# Revit family: Casement_41_E_Side_Hung_HD_Standard
name_source: partatom
category: Windows
revit_build: Autodesk Revit 2014 (Build: 20130308_1515(x64)
units: mm (PartAtom-declared; Revit-internal decimal feet)

## types (18) — shared parameters
Corrected Mullion Configuration = 2 mm  [stored 0.00656168 ft]
Custom Sash Height = 1102 mm
Custom Sash Width = 502 mm
Description = Window 41mm, Type E, Side hung, Heavy duty sash
Frame Profile Thickness = 41 mm  [stored 0.134514 ft]
Heavy Duty Sash = Yes
Limit Fixed Pane Height Max = 3000 mm  [stored 9.84252 ft]
Limit Fixed Pane Height Min = 200 mm  [stored 0.656168 ft]
Limit Fixed Pane Width Max = 3000 mm  [stored 9.84252 ft]
Limit Fixed Pane Width Min = 200 mm  [stored 0.656168 ft]
Limit Sash Height Max = 1500 mm  [stored 4.92126 ft]
Limit Sash Height Min = 300 mm  [stored 0.984252 ft]
Limit Sash Width Max = 700 mm  [stored 2.29659 ft]
Limit Sash Width Min = 300 mm  [stored 0.984252 ft]
Manufacturer = Crealco
Max System DG Unit Thickness = 25 mm  [stored 0.082021 ft]
Model = Casement 41
Rough Width = 3 mm  [stored 0.00984252 ft]
Sash Side Gap = 44 mm
Standard Mullion Different = No
Standard Sash = No
URL = http://www.crealco.co.za
Wall Closure = By host
zero-valued in all types: Custom Frame Offset From Exterior

## per-type parameters (varying)
| type | Clearvue Insulated LowE SHGC Value | Clearvue Insulated LowE U Value | Clearvue Insulated SHGC Value | Clearvue Insulated U Value | Clearvue SHGC Value | Clearvue U Value | Custom Windload | Custom Window Height | Custom Window Width | Energy Advantage SHGC Value | Energy Advantage U Value | Intruderprufe Insulated LowE SHGC Value | Intruderprufe Insulated LowE U Value | Intruderprufe Insulated SHGC Value | Intruderprufe Insulated U Value | Intruderprufe LowE SHGC Value | Intruderprufe LowE U Value | Intruderprufe SHGC Value | Intruderprufe U Value | Toughened Safety SHGC Value | Toughened Safety U Value |
| 41-0915S-HD-1000Pa | 0.699 | 4.27 | 0.699 | 4.38 | 0.517 | 6.07 | 1000 mm  [stored 3.28084 ft] | 1490 mm  [stored 4.88845 ft] | 890 mm  [stored 2.91995 ft] | 0.466 | 4.99 | 0.581 | 3.25 | 0.581 | 3.32 | 0.433 | 4.83 | 0.487 | 5.9 | 0.517 | 6.07 |
| 41-0915S-HD-1500Pa | 0.699 | 4.27 | 0.699 | 4.38 | 0.517 | 6.07 | 1500 mm  [stored 4.92126 ft] | 1490 mm  [stored 4.88845 ft] | 890 mm  [stored 2.91995 ft] | 0.466 | 4.99 | 0.581 | 3.25 | 0.581 | 3.32 | 0.433 | 4.83 | 0.487 | 5.9 | 0.517 | 6.07 |
| 41-0915S-HD-2000Pa | 0.699 | 4.27 | 0.699 | 4.38 | 0.517 | 6.07 | 2000 mm  [stored 6.56168 ft] | 1490 mm  [stored 4.88845 ft] | 890 mm  [stored 2.91995 ft] | 0.466 | 4.99 | 0.581 | 3.25 | 0.581 | 3.32 | 0.433 | 4.83 | 0.487 | 5.9 | 0.517 | 6.07 |
| 41-1215S-HD-1000Pa | 0.737 | 4.55 | 0.737 | 4.63 | 0.585 | 6.04 | 1000 mm  [stored 3.28084 ft] | 1490 mm  [stored 4.88845 ft] | 1190 mm  [stored 3.9042 ft] | 0.526 | 4.73 | 0.612 | 3.27 | 0.612 | 3.32 | 0.489 | 4.58 | 0.551 | 5.86 | 0.585 | 6.04 |
| 41-1215S-HD-1500Pa | 0.737 | 4.55 | 0.737 | 4.63 | 0.585 | 6.04 | 1500 mm  [stored 4.92126 ft] | 1490 mm  [stored 4.88845 ft] | 1190 mm  [stored 3.9042 ft] | 0.526 | 4.73 | 0.612 | 3.27 | 0.612 | 3.32 | 0.489 | 4.58 | 0.551 | 5.86 | 0.585 | 6.04 |
| 41-1215S-HD-2000Pa | 0.738 | 4.69 | 0.738 | 4.77 | 0.576 | 6.1 | 2000 mm  [stored 6.56168 ft] | 1490 mm  [stored 4.88845 ft] | 1190 mm  [stored 3.9042 ft] | 0.518 | 4.84 | 0.614 | 3.4 | 0.614 | 3.45 | 0.481 | 4.68 | 0.542 | 5.92 | 0.576 | 6.1 |
| 41-1515S-HD-1000Pa | 0.76 | 4.72 | 0.76 | 4.78 | 0.626 | 6.01 | 1000 mm  [stored 3.28084 ft] | 1490 mm  [stored 4.88845 ft] | 1490 mm  [stored 4.88845 ft] | 0.561 | 4.58 | 0.631 | 3.28 | 0.631 | 3.32 | 0.522 | 4.43 | 0.589 | 5.84 | 0.626 | 6.01 |
| 41-1515S-HD-1500Pa | 0.76 | 4.72 | 0.76 | 4.78 | 0.626 | 6.01 | 1500 mm  [stored 4.92126 ft] | 1490 mm  [stored 4.88845 ft] | 1490 mm  [stored 4.88845 ft] | 0.561 | 4.58 | 0.631 | 3.28 | 0.631 | 3.32 | 0.522 | 4.43 | 0.589 | 5.84 | 0.626 | 6.01 |
| 41-1515S-HD-2000Pa | 0.761 | 4.83 | 0.761 | 4.89 | 0.619 | 6.07 | 2000 mm  [stored 6.56168 ft] | 1490 mm  [stored 4.88845 ft] | 1490 mm  [stored 4.88845 ft] | 0.555 | 4.66 | 0.632 | 3.38 | 0.632 | 3.42 | 0.516 | 4.51 | 0.582 | 5.89 | 0.619 | 6.07 |
| 41-0918S-HD-1000Pa | 0.708 | 4.33 | 0.708 | 4.44 | 0.54 | 6.06 | 1000 mm  [stored 3.28084 ft] | 1790 mm  [stored 5.8727 ft] | 890 mm  [stored 2.91995 ft] | 0.486 | 4.91 | 0.589 | 3.26 | 0.589 | 3.33 | 0.452 | 4.74 | 0.508 | 5.87 | 0.54 | 6.06 |
| 41-0918S-HD-1500Pa | 0.71 | 4.52 | 0.71 | 4.62 | 0.523 | 6.16 | 1500 mm  [stored 4.92126 ft] | 1790 mm  [stored 5.8727 ft] | 890 mm  [stored 2.91995 ft] | 0.471 | 5.07 | 0.591 | 3.44 | 0.591 | 3.5 | 0.438 | 4.89 | 0.492 | 5.96 | 0.523 | 6.16 |
| 41-0918S-HD-2000Pa | 0.71 | 4.52 | 0.71 | 4.62 | 0.523 | 6.16 | 2000 mm  [stored 6.56168 ft] | 1790 mm  [stored 5.8727 ft] | 890 mm  [stored 2.91995 ft] | 0.471 | 5.07 | 0.591 | 3.44 | 0.591 | 3.5 | 0.438 | 4.89 | 0.492 | 5.96 | 0.523 | 6.16 |
| 41-1218S-HD-1000Pa | 0.744 | 4.62 | 0.744 | 4.7 | 0.605 | 6.03 | 1000 mm  [stored 3.28084 ft] | 1790 mm  [stored 5.8727 ft] | 1190 mm  [stored 3.9042 ft] | 0.543 | 4.66 | 0.618 | 3.29 | 0.618 | 3.34 | 0.505 | 4.5 | 0.569 | 5.84 | 0.605 | 6.03 |
| 41-1218S-HD-1500Pa | 0.745 | 4.76 | 0.745 | 4.83 | 0.592 | 6.1 | 1500 mm  [stored 4.92126 ft] | 1790 mm  [stored 5.8727 ft] | 1190 mm  [stored 3.9042 ft] | 0.532 | 4.78 | 0.619 | 3.42 | 0.619 | 3.47 | 0.494 | 4.62 | 0.557 | 5.91 | 0.592 | 6.1 |
| 41-1218S-HD-2000Pa | 0.745 | 4.76 | 0.745 | 4.83 | 0.592 | 6.1 | 2000 mm  [stored 6.56168 ft] | 1790 mm  [stored 5.8727 ft] | 1190 mm  [stored 3.9042 ft] | 0.532 | 4.78 | 0.619 | 3.42 | 0.619 | 3.47 | 0.494 | 4.62 | 0.557 | 5.91 | 0.592 | 6.1 |
| 41-1518S-HD-1000Pa | 0.766 | 4.9 | 0.766 | 4.96 | 0.633 | 6.06 | 1000 mm  [stored 3.28084 ft] | 1790 mm  [stored 5.8727 ft] | 1490 mm  [stored 4.88845 ft] | 0.568 | 4.61 | 0.637 | 3.41 | 0.637 | 3.45 | 0.528 | 4.45 | 0.596 | 5.87 | 0.633 | 6.06 |
| 41-1518S-HD-1500Pa | 0.766 | 4.9 | 0.766 | 4.96 | 0.633 | 6.06 | 1500 mm  [stored 4.92126 ft] | 1790 mm  [stored 5.8727 ft] | 1490 mm  [stored 4.88845 ft] | 0.568 | 4.61 | 0.637 | 3.41 | 0.637 | 3.45 | 0.528 | 4.45 | 0.596 | 5.87 | 0.633 | 6.06 |
| 41-1518S-HD-2000Pa | 0.766 | 4.9 | 0.766 | 4.96 | 0.633 | 6.06 | 2000 mm  [stored 6.56168 ft] | 1790 mm  [stored 5.8727 ft] | 1490 mm  [stored 4.88845 ft] | 0.568 | 4.61 | 0.637 | 3.41 | 0.637 | 3.45 | 0.528 | 4.45 | 0.596 | 5.87 | 0.633 | 6.06 |

note: [stored X ft] marks values corroborated as IEEE doubles in the binary element streams (Revit-internal decimal feet)

## geometry (parser evidence)
native form markers: Sweep x11
no freeform markers — native parametric forms only
